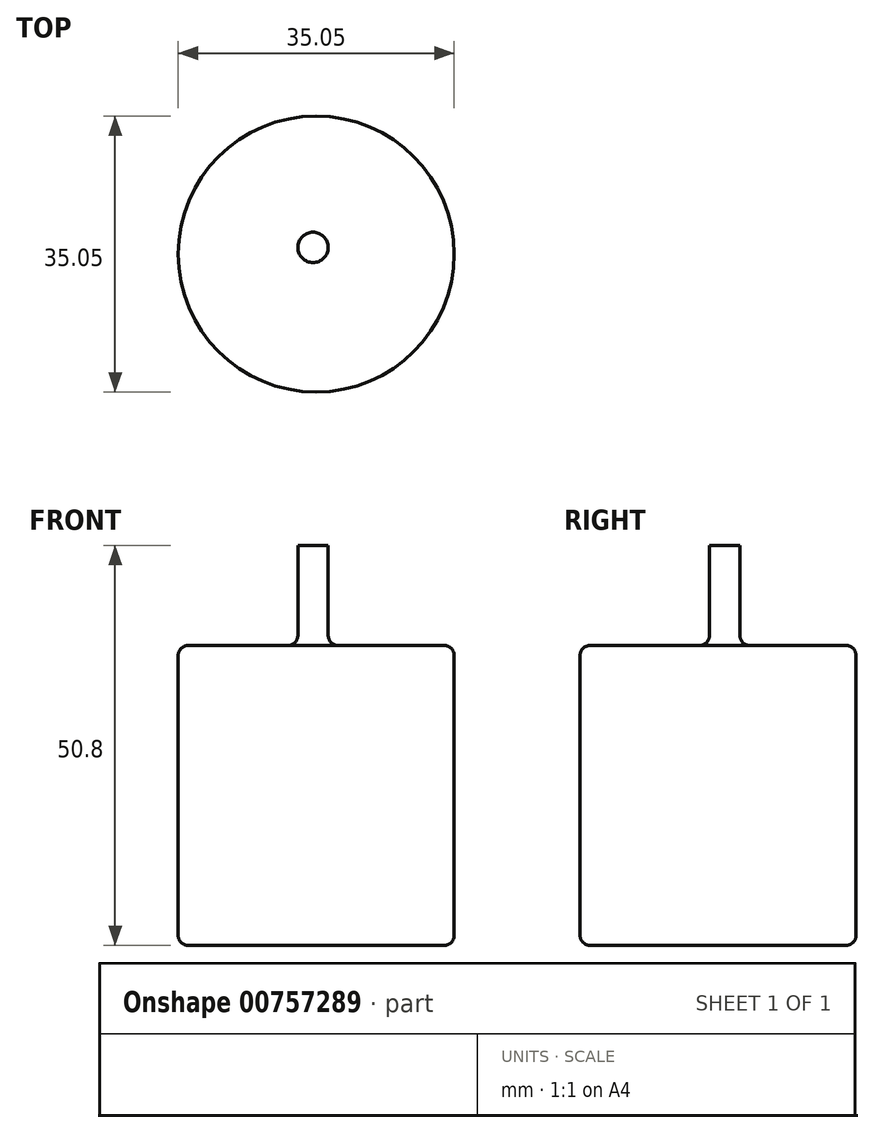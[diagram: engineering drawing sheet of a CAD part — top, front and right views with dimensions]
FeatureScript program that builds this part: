
annotation { "Feature Type Name" : "Feature", "Feature Type Description" : "" }
export const myFeature = defineFeature(function(context is Context, id is Id, definition is map)
    precondition{}
    {
        {
            var Q0;
            Q0=qCreatedBy(makeId("Top.planeOp"),FACE);
            var sketch = newSketch(context, id + "F0", { "sketchPlane" : qUnion([Q0])});
            skCircle(sketch, "E0", {"center": v(-59.54, 23.27) * mm, "radius": 17.53 * mm});
            skSolve(sketch);
        }
        {
            var Q0;
            Q0 = qSketchRegion(id + "F0", true);
            extrude(context, id + "F1", {"entities" : qUnion([Q0]), "depth" : 38.1 * mm, "offsetDistance" : 25.4 * mm});
        }
        {
            var Q0;
            Q0=qCreatedBy(makeId("Top.planeOp"),FACE);
            var sketch = newSketch(context, id + "F2", { "sketchPlane" : qUnion([Q0])});
            skCircle(sketch, "E1", {"center": v(-59.94, 24.12) * mm, "radius": 1.93 * mm});
            skSolve(sketch);
        }
        {
            var Q0;
            Q0 = qSketchRegion(id + "F2", true);
            extrude(context, id + "F3", {"entities" : qUnion([Q0]), "operationType" : NewBodyOperationType.ADD, "depth" : 50.8 * mm, "offsetDistance" : 25.4 * mm});
        }
        {
            var Q0;
            Q0=makeQuery(id+"F1.opExtrude","CAP_FACE",FACE,{"disambiguationData":[OSD([sQuery(id+"F0.wireOp",EDGE,"E0")])],"isStart":false});
            var Q1;
            Q1=makeQuery(id+"F1.opExtrude","CAP_FACE",FACE,{"disambiguationData":[OSD([sQuery(id+"F0.wireOp",EDGE,"E0")])],"isStart":true});
            fillet(context, id + "F4", {"entities" : qUnion([Q0, Q1]), "radius" : 1.27 * mm, "tangentPropagation" : true, "allowEdgeOverflow" : false});
        }
    });
